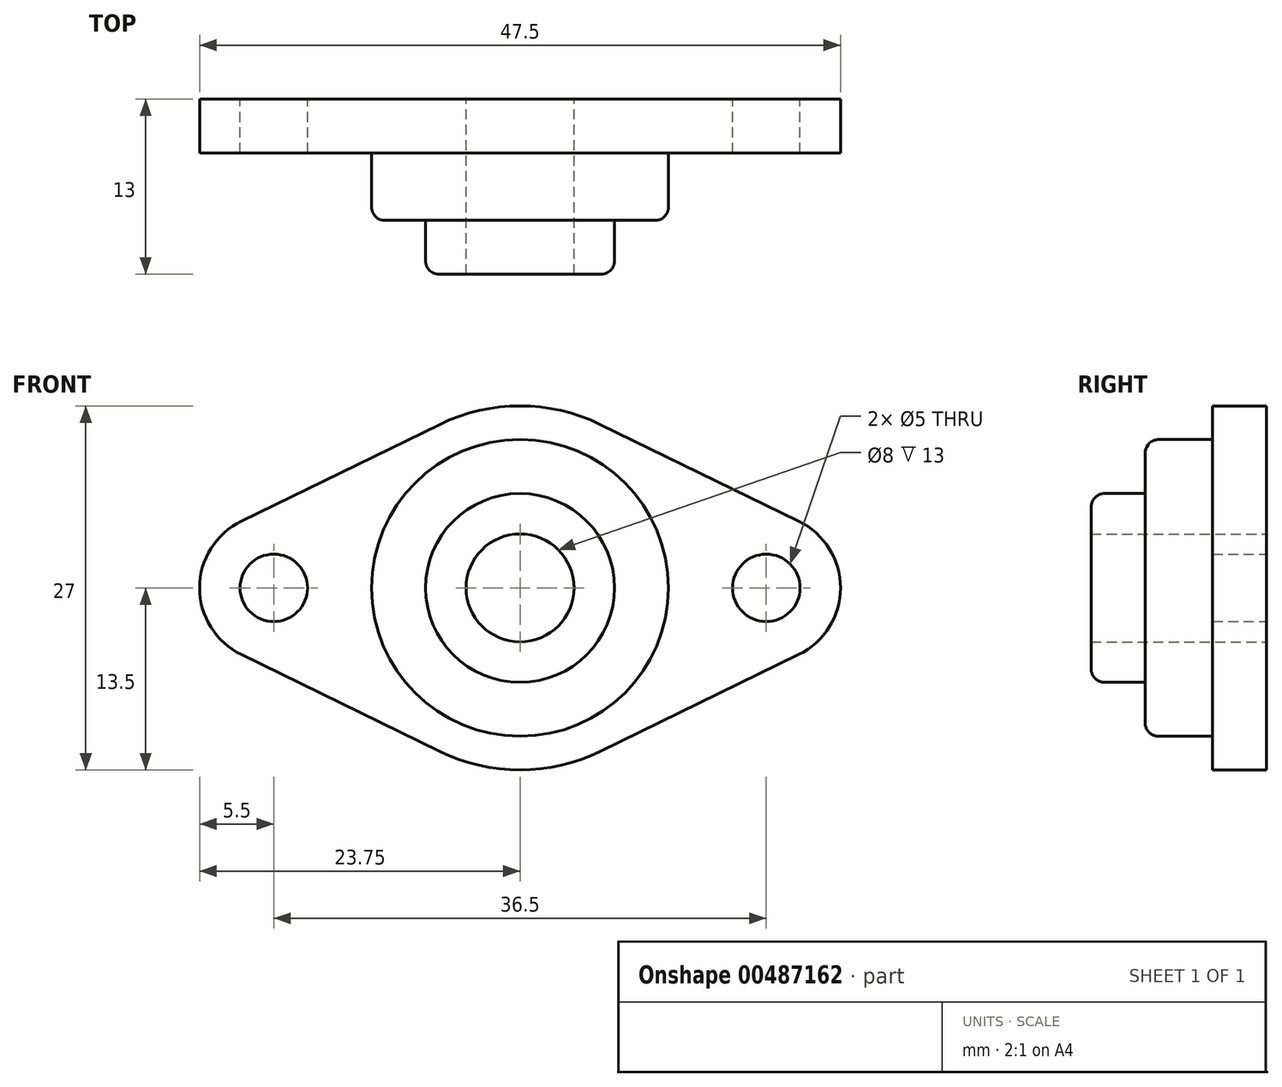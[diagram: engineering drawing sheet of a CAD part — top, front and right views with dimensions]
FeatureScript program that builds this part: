
annotation { "Feature Type Name" : "Feature", "Feature Type Description" : "" }
export const myFeature = defineFeature(function(context is Context, id is Id, definition is map)
    precondition{}
    {
        {
            var Q0;
            Q0=qCreatedBy(makeId("Front.planeOp"),FACE);
            var sketch = newSketch(context, id + "F0", { "sketchPlane" : qUnion([Q0])});
            skCircle(sketch, "E0", {"center": v(0, 0) * mm, "radius": 4 * mm});
            skArc(sketch, "E1", {"start": v(-5.92, -12.13) * mm, "mid": v(0, -13.5) * mm, "end": v(5.92, -12.13) * mm});
            skCircle(sketch, "E2", {"center": v(-18.25, 0) * mm, "radius": 2.5 * mm});
            skCircle(sketch, "E3", {"center": v(18.25, 0) * mm, "radius": 2.5 * mm});
            skArc(sketch, "E4", {"start": v(20.66, -4.94) * mm, "mid": v(23.75, 0) * mm, "end": v(20.66, 4.94) * mm});
            skArc(sketch, "E5", {"start": v(-20.66, 4.94) * mm, "mid": v(-23.75, 0) * mm, "end": v(-20.66, -4.94) * mm});
            skLineSegment(sketch, "E6", {"start": v(-20.66, 4.94) * mm, "end": v(-5.92, 12.13) * mm});
            skLineSegment(sketch, "E7", {"start": v(-20.66, -4.94) * mm, "end": v(-5.92, -12.13) * mm});
            skLineSegment(sketch, "E8", {"start": v(5.92, -12.13) * mm, "end": v(20.66, -4.94) * mm});
            skLineSegment(sketch, "E9", {"start": v(20.66, 4.94) * mm, "end": v(5.92, 12.13) * mm});
            skArc(sketch, "E10.trimOffspring", {"start": v(5.92, 12.13) * mm, "mid": v(0, 13.5) * mm, "end": v(-5.92, 12.13) * mm});
            skSolve(sketch);
        }
        {
            var Q0;
            Q0 = qSketchRegion(id + "F0", true);
            extrude(context, id + "F1", {"entities" : qUnion([Q0]), "depth" : 4 * mm});
        }
        {
            var Q0;
            Q0=makeQuery(id+"F1.opExtrude","CAP_FACE",FACE,{"disambiguationData":[OSD([sQuery(id+"F0.wireOp",EDGE,"E0"),sQuery(id+"F0.wireOp",EDGE,"E1"),sQuery(id+"F0.wireOp",EDGE,"E2"),sQuery(id+"F0.wireOp",EDGE,"E3"),sQuery(id+"F0.wireOp",EDGE,"E4"),sQuery(id+"F0.wireOp",EDGE,"E5"),sQuery(id+"F0.wireOp",EDGE,"E6"),sQuery(id+"F0.wireOp",EDGE,"E7"),sQuery(id+"F0.wireOp",EDGE,"E8"),sQuery(id+"F0.wireOp",EDGE,"E9"),sQuery(id+"F0.wireOp",EDGE,"E10.trimOffspring")])],"isStart":false});
            var sketch = newSketch(context, id + "F2", { "sketchPlane" : qUnion([Q0])});
            skCircle(sketch, "E11", {"center": v(0, 0) * mm, "radius": 4 * mm});
            skCircle(sketch, "E12", {"center": v(0, 0) * mm, "radius": 11 * mm});
            skSolve(sketch);
        }
        {
            var Q0;
            Q0 = qSketchRegion(id + "F2", true);
            extrude(context, id + "F3", {"entities" : qUnion([Q0]), "operationType" : NewBodyOperationType.ADD, "depth" : 5 * mm});
        }
        {
            var Q0;
            Q0=makeQuery(id+"F3.opExtrude","CAP_FACE",FACE,{"disambiguationData":[OSD([sQuery(id+"F2.wireOp",EDGE,"E11"),sQuery(id+"F2.wireOp",EDGE,"E12")])],"isStart":false});
            var sketch = newSketch(context, id + "F4", { "sketchPlane" : qUnion([Q0])});
            skCircle(sketch, "E13", {"center": v(0, 0) * mm, "radius": 4 * mm});
            skCircle(sketch, "E14", {"center": v(0, 0) * mm, "radius": 7 * mm});
            skSolve(sketch);
        }
        {
            var Q0;
            Q0 = qSketchRegion(id + "F4", true);
            extrude(context, id + "F5", {"entities" : qUnion([Q0]), "operationType" : NewBodyOperationType.ADD, "depth" : 4 * mm});
        }
        {
            var Q0;
            Q0=makeQuery(id+"F3.opExtrude","CAP_EDGE",EDGE,{"disambiguationData":[OSD([sQuery(id+"F2.wireOp",EDGE,"E12")])],"isStart":false});
            var Q1;
            Q1=makeQuery(id+"F5.opExtrude","CAP_EDGE",EDGE,{"disambiguationData":[OSD([sQuery(id+"F4.wireOp",EDGE,"E14")])],"isStart":true});
            var Q2;
            Q2=makeQuery(id+"F3.opExtrude","CAP_EDGE",EDGE,{"disambiguationData":[OSD([sQuery(id+"F2.wireOp",EDGE,"E12")])],"isStart":true});
            var Q3;
            Q3=makeQuery(id+"F5.opExtrude","CAP_EDGE",EDGE,{"disambiguationData":[OSD([sQuery(id+"F4.wireOp",EDGE,"E14")])],"isStart":false});
            fillet(context, id + "F6", {"entities" : qUnion([Q0, Q1, Q2, Q3]), "radius" : 1 * mm, "tangentPropagation" : true, "allowEdgeOverflow" : false});
        }
    });
